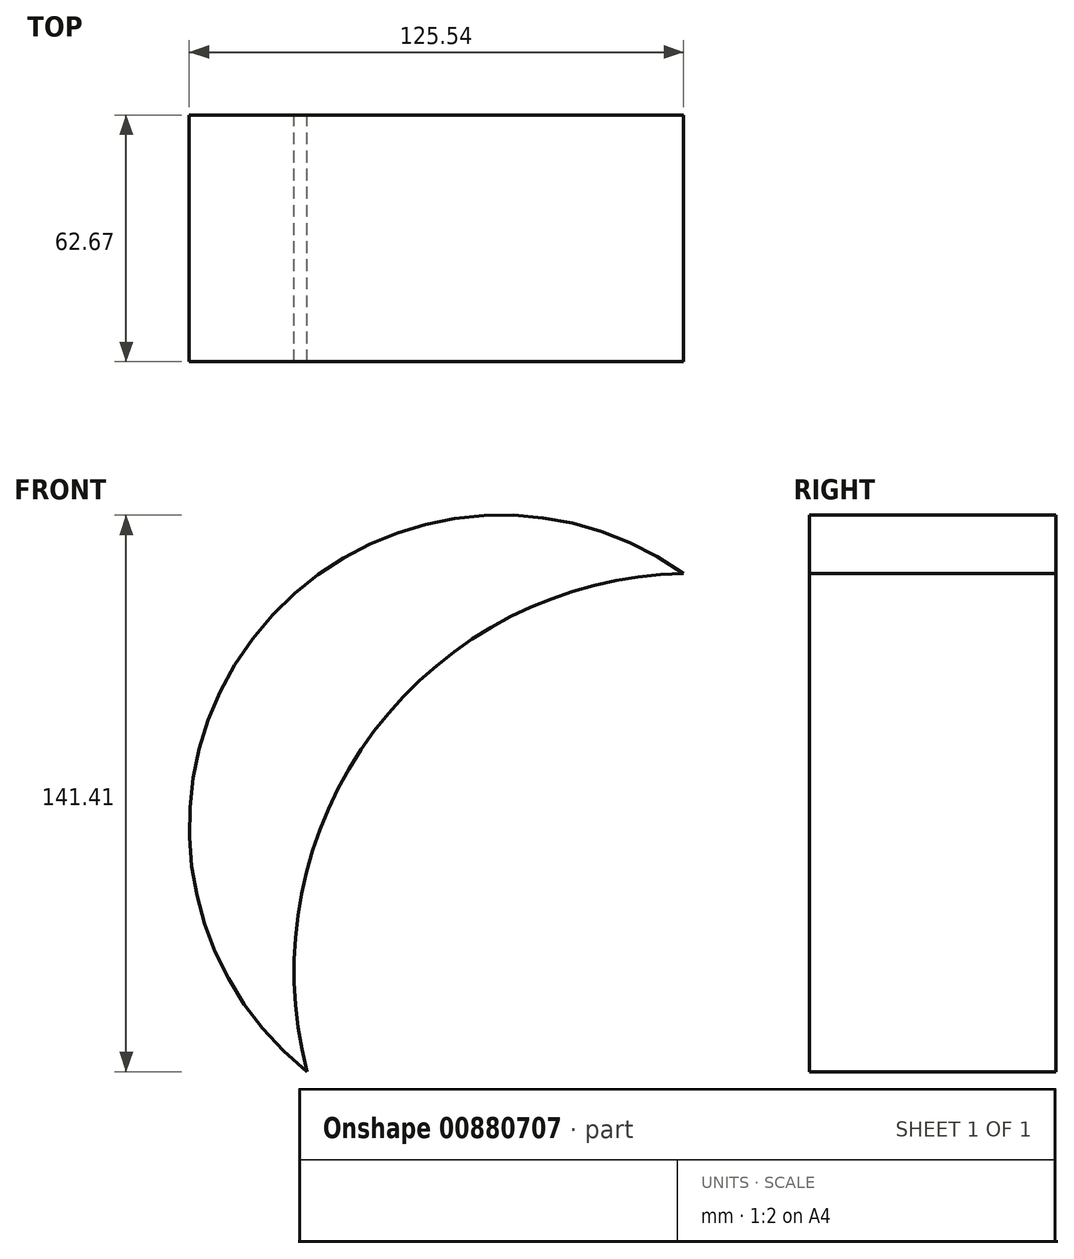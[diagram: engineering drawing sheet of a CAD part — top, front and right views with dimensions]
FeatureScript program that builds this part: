
annotation { "Feature Type Name" : "Feature", "Feature Type Description" : "" }
export const myFeature = defineFeature(function(context is Context, id is Id, definition is map)
    precondition{}
    {
        {
            var Q0;
            Q0=qCreatedBy(makeId("Front.planeOp"),FACE);
            var sketch = newSketch(context, id + "F0", { "sketchPlane" : qUnion([Q0])});
            skArc(sketch, "E0", {"start": v(17.5, 107.46) * mm, "mid": v(-115.47, 128.73) * mm, "end": v(-75.96, 0) * mm});
            skArc(sketch, "E1", {"start": v(-46.94, -72.86) * mm, "mid": v(23.88, -1.44) * mm, "end": v(-75.96, -13.68) * mm});
            skArc(sketch, "E2", {"start": v(76.38, 96.3) * mm, "mid": v(-107.94, 31.44) * mm, "end": v(84.92, 0) * mm});
            skSolve(sketch);
        }
        {
            var Q0;
            {var subQ0=sQuery(id+"F0.wireOp",EDGE,"E2");var subQ1=sQuery(id+"F0.wireOp",EDGE,"E0");var subQ2=makeQuery(id+"F0.imprint","INTERSECT",VERTEX,{"disambiguationData":[OD(0.0)],"derivedFrom":[subQ1,subQ0]});Q0=makeQuery(id+"F0.imprint","IMPRINT",FACE,{"disambiguationData":[TD([[makeQuery(id+"F0.imprint","IMPRINT",EDGE,{"disambiguationData":[TD([[subQ2,1.0]])],"derivedFrom":subQ1}),1.0]])]});}
            extrude(context, id + "F1", {"entities" : qUnion([Q0]), "depth" : 25.4 * mm, "offsetDistance" : 25.4 * mm});
        }
        {
            var Q0;
            Q0=makeQuery(id+"F1.opExtrude","CAP_FACE",FACE,{"disambiguationData":[OSD([sQuery(id+"F0.wireOp",EDGE,"E0"),sQuery(id+"F0.wireOp",EDGE,"E2")])],"isStart":true});
            extrude(context, id + "F2", {"entities" : qUnion([Q0]), "operationType" : NewBodyOperationType.ADD, "depth" : 37.27 * mm, "offsetDistance" : 25.4 * mm});
        }
    });
